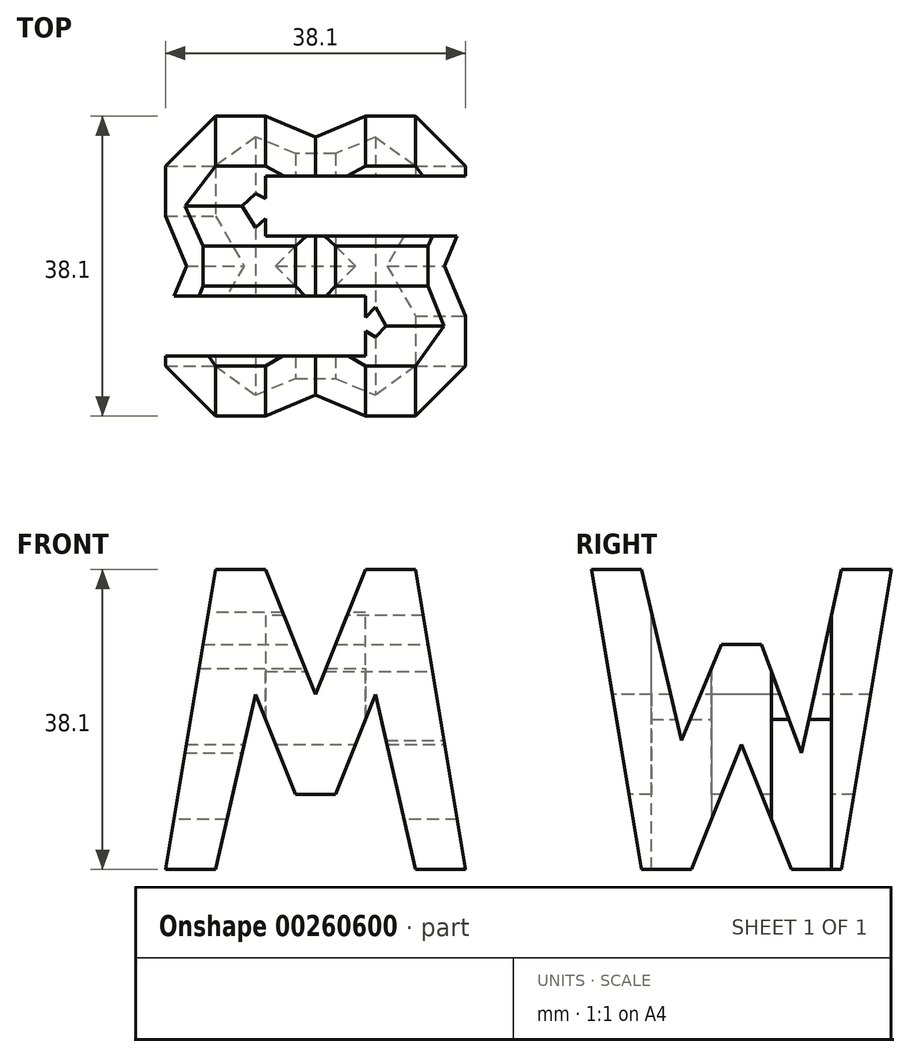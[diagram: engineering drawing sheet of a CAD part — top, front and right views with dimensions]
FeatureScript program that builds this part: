
annotation { "Feature Type Name" : "Feature", "Feature Type Description" : "" }
export const myFeature = defineFeature(function(context is Context, id is Id, definition is map)
    precondition{}
    {
        {
            var Q0;
            Q0=qCreatedBy(makeId("Front.planeOp"),FACE);
            var sketch = newSketch(context, id + "F0", { "sketchPlane" : qUnion([Q0])});
            skLineSegment(sketch, "E0", {"start": v(0, 0) * mm, "end": v(0, 38.1) * mm});
            skLineSegment(sketch, "E1", {"start": v(0, 38.1) * mm, "end": v(38.1, 38.1) * mm});
            skLineSegment(sketch, "E2", {"start": v(38.1, 38.1) * mm, "end": v(38.1, 0) * mm});
            skLineSegment(sketch, "E3", {"start": v(38.1, 0) * mm, "end": v(0, 0) * mm});
            skSolve(sketch);
        }
        {
            var Q0;
            Q0 = qSketchRegion(id + "F0", true);
            extrude(context, id + "F1", {"entities" : qUnion([Q0]), "depth" : 38.1 * mm});
        }
        {
            var Q0;
            Q0=qCreatedBy(makeId("Front.planeOp"),FACE);
            cPlane(context, id + "F2", {"entities" : qUnion([Q0]), "cplaneType" : CPlaneType.OFFSET, "offset" : 38.1 * mm, "width" : 152.4 * mm, "height" : 152.4 * mm});
        }
        {
            var Q0;
            Q0=qCreatedBy(makeId("Right.planeOp"),FACE);
            cPlane(context, id + "F3", {"entities" : qUnion([Q0]), "cplaneType" : CPlaneType.OFFSET, "offset" : 38.1 * mm, "width" : 152.4 * mm, "height" : 152.4 * mm});
        }
        {
            var Q0;
            Q0=qCreatedBy(makeId("Top.planeOp"),FACE);
            cPlane(context, id + "F4", {"entities" : qUnion([Q0]), "cplaneType" : CPlaneType.OFFSET, "offset" : 38.1 * mm, "width" : 152.4 * mm, "height" : 152.4 * mm});
        }
        {
            var Q0;
            Q0=qCreatedBy(id+"F3.planeOp",FACE);
            var sketch = newSketch(context, id + "F5", { "sketchPlane" : qUnion([Q0])});
            skLineSegment(sketch, "E4.bottom", {"start": v(0, 0) * mm, "end": v(-38.1, 0) * mm});
            skLineSegment(sketch, "E4.top", {"start": v(0, 38.1) * mm, "end": v(-38.1, 38.1) * mm});
            skLineSegment(sketch, "E4.left", {"start": v(0, 0) * mm, "end": v(0, 38.1) * mm});
            skLineSegment(sketch, "E4.right", {"start": v(-38.1, 0) * mm, "end": v(-38.1, 38.1) * mm});
            skLineSegment(sketch, "E5", {"start": v(-38.1, 38.1) * mm, "end": v(-31.75, 0) * mm});
            skLineSegment(sketch, "E6", {"start": v(-31.75, 0) * mm, "end": v(-25.4, 0) * mm});
            skLineSegment(sketch, "E7", {"start": v(-25.4, 0) * mm, "end": v(-19.05, 15.88) * mm});
            skLineSegment(sketch, "E8", {"start": v(-19.05, 15.88) * mm, "end": v(-12.7, 0) * mm});
            skLineSegment(sketch, "E9", {"start": v(-12.7, 0) * mm, "end": v(-6.35, 0) * mm});
            skLineSegment(sketch, "E10", {"start": v(-6.35, 0) * mm, "end": v(0, 38.1) * mm});
            skLineSegment(sketch, "E11", {"start": v(-6.35, 38.1) * mm, "end": v(-11.43, 14.8) * mm});
            skLineSegment(sketch, "E12", {"start": v(-11.43, 14.8) * mm, "end": v(-16.5, 28.57) * mm});
            skLineSegment(sketch, "E13", {"start": v(-16.5, 28.57) * mm, "end": v(-21.59, 28.57) * mm});
            skLineSegment(sketch, "E14", {"start": v(-21.59, 28.57) * mm, "end": v(-26.67, 16.39) * mm});
            skLineSegment(sketch, "E15", {"start": v(-26.67, 16.39) * mm, "end": v(-31.75, 38.1) * mm});
            skLineSegment(sketch, "E16", {"start": v(-31.75, 38.1) * mm, "end": v(-38.1, 38.1) * mm});
            skSolve(sketch);
        }
        {
            var Q0;
            {var subQ0=sQuery(id+"F5.wireOp",EDGE,"E11");Q0=makeQuery(id+"F5.imprint","IMPRINT",FACE,{"disambiguationData":[TD([[makeQuery(id+"F5.imprint","IMPRINT",EDGE,{"derivedFrom":subQ0}),-1.0]])]});}
            var Q1;
            {var subQ0=sQuery(id+"F5.wireOp",EDGE,"E7");Q1=makeQuery(id+"F5.imprint","IMPRINT",FACE,{"disambiguationData":[TD([[makeQuery(id+"F5.imprint","IMPRINT",EDGE,{"derivedFrom":subQ0}),-1.0]])]});}
            var Q2;
            {var subQ0=sQuery(id+"F5.wireOp",EDGE,"E4.right");Q2=makeQuery(id+"F5.imprint","IMPRINT",FACE,{"disambiguationData":[TD([[makeQuery(id+"F5.imprint","IMPRINT",EDGE,{"derivedFrom":subQ0}),-1.0]])]});}
            var Q3;
            {var subQ0=sQuery(id+"F5.wireOp",EDGE,"E4.left");Q3=makeQuery(id+"F5.imprint","IMPRINT",FACE,{"disambiguationData":[TD([[makeQuery(id+"F5.imprint","IMPRINT",EDGE,{"derivedFrom":subQ0}),1.0]])]});}
            extrude(context, id + "F6", {"entities" : qUnion([Q0, Q1, Q2, Q3]), "operationType" : NewBodyOperationType.REMOVE, "oppositeDirection" : true, "depth" : 38.1 * mm});
        }
        {
            var Q0;
            Q0=qCreatedBy(id+"F2.planeOp",FACE);
            var sketch = newSketch(context, id + "F7", { "sketchPlane" : qUnion([Q0])});
            skLineSegment(sketch, "E17", {"start": v(0, 0) * mm, "end": v(6.35, 38.1) * mm});
            skLineSegment(sketch, "E18", {"start": v(12.7, 38.1) * mm, "end": v(19.05, 22.23) * mm});
            skLineSegment(sketch, "E19", {"start": v(19.05, 22.23) * mm, "end": v(25.4, 38.1) * mm});
            skLineSegment(sketch, "E20", {"start": v(31.75, 38.1) * mm, "end": v(38.1, 0) * mm});
            skLineSegment(sketch, "E21", {"start": v(31.75, 0) * mm, "end": v(26.67, 22.22) * mm});
            skLineSegment(sketch, "E22", {"start": v(6.35, 0) * mm, "end": v(11.43, 22.23) * mm});
            skLineSegment(sketch, "E23", {"start": v(11.43, 22.23) * mm, "end": v(16.51, 9.53) * mm});
            skLineSegment(sketch, "E24", {"start": v(16.51, 9.53) * mm, "end": v(21.6, 9.53) * mm});
            skLineSegment(sketch, "E25", {"start": v(21.6, 9.53) * mm, "end": v(26.67, 22.22) * mm});
            skLineSegment(sketch, "E26", {"start": v(0, 0) * mm, "end": v(0, 38.1) * mm});
            skLineSegment(sketch, "E27", {"start": v(0, 38.1) * mm, "end": v(38.1, 38.1) * mm});
            skLineSegment(sketch, "E28", {"start": v(38.1, 38.1) * mm, "end": v(38.1, 0) * mm});
            skLineSegment(sketch, "E29", {"start": v(38.1, 0) * mm, "end": v(0, 0) * mm});
            skLineSegment(sketch, "E30.bottom", {"start": v(0, 0) * mm, "end": v(38.1, 0) * mm});
            skLineSegment(sketch, "E30.right", {"start": v(38.1, 0) * mm, "end": v(38.1, 38.1) * mm});
            skSolve(sketch);
        }
        {
            var Q0;
            {var subQ1=sQuery(id+"F7.wireOp",EDGE,"E21");Q0=makeQuery(id+"F7.imprint","IMPRINT",FACE,{"disambiguationData":[TD([[makeQuery(id+"F7.imprint","IMPRINT",EDGE,{"derivedFrom":subQ1}),1.0]])]});}
            var Q1;
            {var subQ0=sQuery(id+"F7.wireOp",EDGE,"E17");Q1=makeQuery(id+"F7.imprint","IMPRINT",FACE,{"disambiguationData":[TD([[makeQuery(id+"F7.imprint","IMPRINT",EDGE,{"derivedFrom":subQ0}),1.0]])]});}
            var Q2;
            {var subQ0=sQuery(id+"F7.wireOp",EDGE,"E18");Q2=makeQuery(id+"F7.imprint","IMPRINT",FACE,{"disambiguationData":[TD([[makeQuery(id+"F7.imprint","IMPRINT",EDGE,{"derivedFrom":subQ0}),1.0]])]});}
            var Q3;
            {var subQ0=sQuery(id+"F7.wireOp",EDGE,"E20");Q3=makeQuery(id+"F7.imprint","IMPRINT",FACE,{"disambiguationData":[TD([[makeQuery(id+"F7.imprint","IMPRINT",EDGE,{"derivedFrom":subQ0}),1.0]])]});}
            extrude(context, id + "F8", {"entities" : qUnion([Q0, Q1, Q2, Q3]), "operationType" : NewBodyOperationType.REMOVE, "oppositeDirection" : true, "depth" : 38.1 * mm});
        }
        {
            var Q0;
            Q0=qCreatedBy(id+"F4.planeOp",FACE);
            var sketch = newSketch(context, id + "F9", { "sketchPlane" : qUnion([Q0])});
            skLineSegment(sketch, "E31", {"start": v(0, 0) * mm, "end": v(0, -38.1) * mm});
            skLineSegment(sketch, "E32", {"start": v(0, -38.1) * mm, "end": v(38.1, -38.1) * mm});
            skLineSegment(sketch, "E33", {"start": v(38.1, -38.1) * mm, "end": v(38.1, 0) * mm});
            skLineSegment(sketch, "E34", {"start": v(38.1, 0) * mm, "end": v(0, 0) * mm});
            skLineSegment(sketch, "E35", {"start": v(38.1, -7.62) * mm, "end": v(12.7, -7.62) * mm});
            skLineSegment(sketch, "E36", {"start": v(12.7, -7.62) * mm, "end": v(12.7, -15.24) * mm});
            skLineSegment(sketch, "E37", {"start": v(0, -22.86) * mm, "end": v(25.4, -22.86) * mm});
            skPoint(sketch, "E37.endSnap0", {"position": v(0, -22.86) * mm});
            skLineSegment(sketch, "E38", {"start": v(25.4, -22.86) * mm, "end": v(25.4, -30.48) * mm});
            skLineSegment(sketch, "E39", {"start": v(25.4, -30.48) * mm, "end": v(0, -30.48) * mm});
            skLineSegment(sketch, "E40", {"start": v(12.7, -15.24) * mm, "end": v(38.1, -15.24) * mm});
            skPoint(sketch, "E41.orphan", {"position": v(12.7, -7.62) * mm});
            skSolve(sketch);
        }
        {
            var Q0;
            {var subQ0=sQuery(id+"F9.wireOp",EDGE,"E35");Q0=makeQuery(id+"F9.imprint","IMPRINT",FACE,{"disambiguationData":[TD([[makeQuery(id+"F9.imprint","IMPRINT",EDGE,{"derivedFrom":subQ0}),1.0]])]});}
            var Q1;
            {var subQ0=sQuery(id+"F9.wireOp",EDGE,"E37");Q1=makeQuery(id+"F9.imprint","IMPRINT",FACE,{"disambiguationData":[TD([[makeQuery(id+"F9.imprint","IMPRINT",EDGE,{"derivedFrom":subQ0}),-1.0]])]});}
            extrude(context, id + "F10", {"entities" : qUnion([Q0, Q1]), "operationType" : NewBodyOperationType.REMOVE, "oppositeDirection" : true, "depth" : 38.1 * mm});
        }
    });
